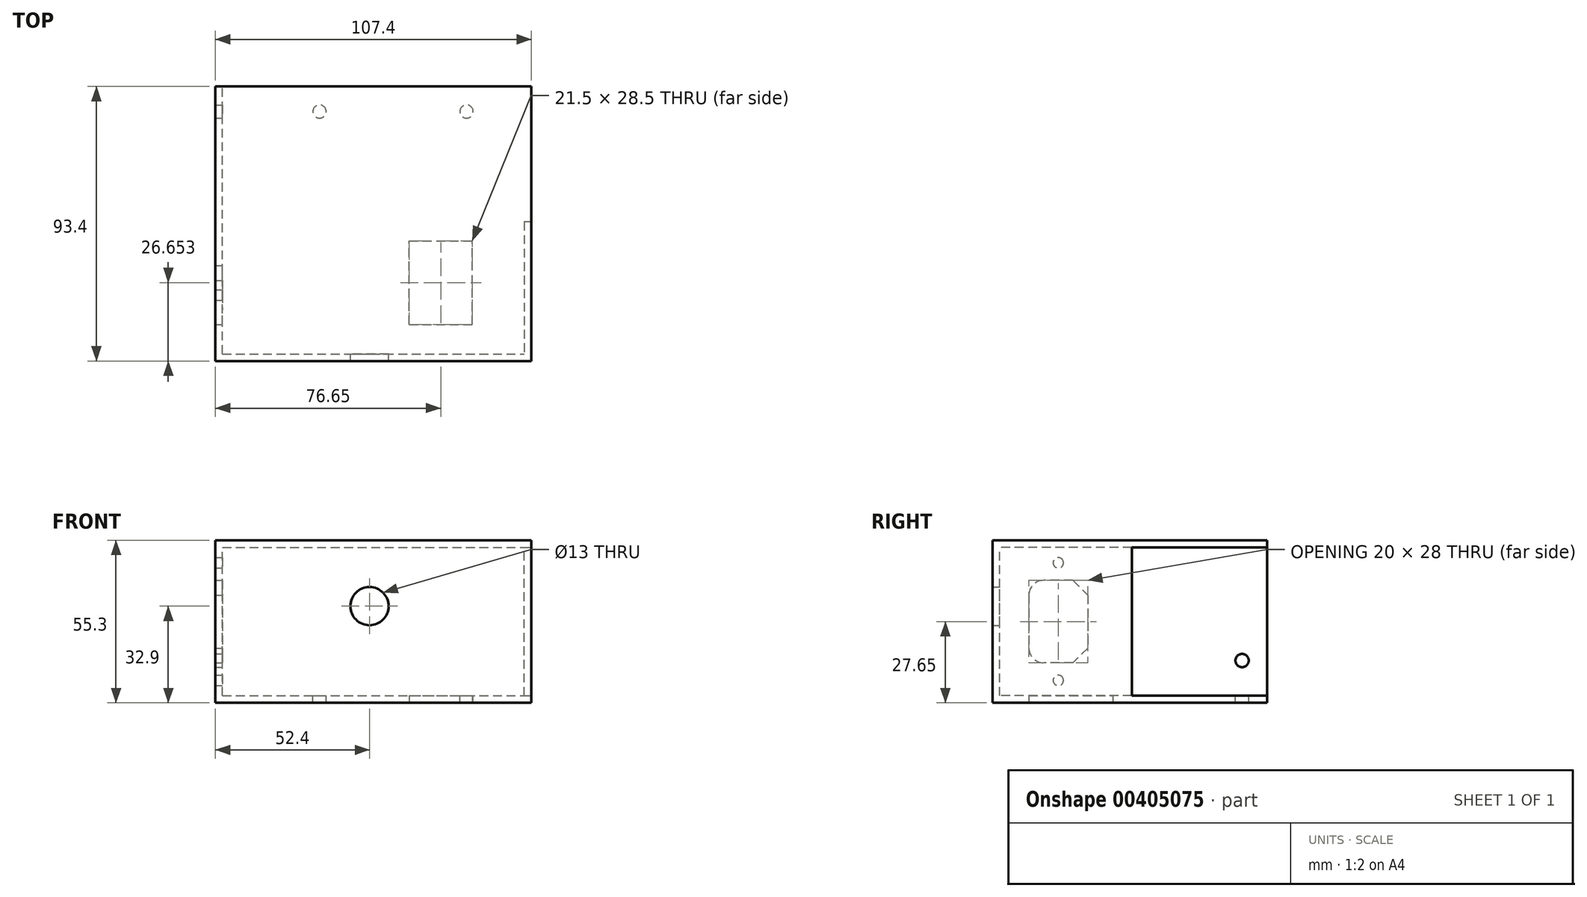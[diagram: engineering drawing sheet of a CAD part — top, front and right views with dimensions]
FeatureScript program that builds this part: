
annotation { "Feature Type Name" : "Feature", "Feature Type Description" : "" }
export const myFeature = defineFeature(function(context is Context, id is Id, definition is map)
    precondition{}
    {
        {
            var Q0;
            Q0=qCreatedBy(makeId("Front.planeOp"),FACE);
            var sketch = newSketch(context, id + "F0", { "sketchPlane" : qUnion([Q0])});
            skLineSegment(sketch, "E0.bottom", {"start": v(-57.5, 25) * mm, "end": v(0, 25) * mm});
            skLineSegment(sketch, "E0.top", {"start": v(-57.5, -25) * mm, "end": v(0, -25) * mm});
            skLineSegment(sketch, "E0.left", {"start": v(-57.5, 25) * mm, "end": v(-57.5, -25) * mm});
            skLineSegment(sketch, "E0.right", {"start": v(0, 25) * mm, "end": v(0, -25) * mm});
            skLineSegment(sketch, "E1", {"start": v(0, 0) * mm, "end": v(0, 48.13) * mm, "construction": true});
            skLineSegment(sketch, "E2", {"start": v(0, 0) * mm, "end": v(-98.9, 0) * mm, "construction": true});
            skPoint(sketch, "E2.endSnap0", {"position": v(0, 0) * mm});
            skSolve(sketch);
        }
        {
            var Q0;
            Q0=makeQuery(id+"F0.imprint","IMPRINT",FACE,{"disambiguationData":[TD([[makeQuery(id+"F0.imprint","IMPRINT",EDGE,{"derivedFrom":sQuery(id+"F0.wireOp",EDGE,"E0.bottom")}),-1.0]])]});
            extrude(context, id + "F1", {"entities" : qUnion([Q0]), "endBound" : BoundingType.SYMMETRIC, "depth" : 215 * mm});
        }
        {
            var Q0;
            Q0=makeQuery(id+"F1.opExtrude","SWEPT_FACE",FACE,{"disambiguationData":[OSD([sQuery(id+"F0.wireOp",EDGE,"E0.bottom")])]});
            var sketch = newSketch(context, id + "F2", { "sketchPlane" : qUnion([Q0])});
            skLineSegment(sketch, "E3.bottom", {"start": v(0, -107.5) * mm, "end": v(-55.8, -107.5) * mm});
            skLineSegment(sketch, "E3.top", {"start": v(0, -88.5) * mm, "end": v(-55.8, -88.5) * mm});
            skLineSegment(sketch, "E3.left", {"start": v(0, -107.5) * mm, "end": v(0, -88.5) * mm});
            skLineSegment(sketch, "E3.right", {"start": v(-55.8, -107.5) * mm, "end": v(-55.8, -88.5) * mm});
            skSolve(sketch);
        }
        {
            var Q0;
            Q0=makeQuery(id+"F2.imprint","IMPRINT",FACE,{"disambiguationData":[TD([[makeQuery(id+"F2.imprint","IMPRINT",EDGE,{"derivedFrom":sQuery(id+"F2.wireOp",EDGE,"E3.bottom")}),1.0]])]});
            extrude(context, id + "F3", {"entities" : qUnion([Q0]), "operationType" : NewBodyOperationType.REMOVE, "oppositeDirection" : true, "depth" : 42 * mm});
        }
        {
            var Q0;
            Q0=makeQuery(id+"F1.opExtrude","SWEPT_FACE",FACE,{"disambiguationData":[OSD([sQuery(id+"F0.wireOp",EDGE,"E0.bottom")])]});
            var sketch = newSketch(context, id + "F4", { "sketchPlane" : qUnion([Q0])});
            skLineSegment(sketch, "E4", {"start": v(-55.8, -107.5) * mm, "end": v(-55.8, 107.5) * mm});
            skLineSegment(sketch, "E5", {"start": v(-55.8, 107.5) * mm, "end": v(-55.5, 107.5) * mm});
            skLineSegment(sketch, "E6", {"start": v(-55.5, 107.5) * mm, "end": v(-55.5, 105.8) * mm});
            skLineSegment(sketch, "E7", {"start": v(-55.5, 105.8) * mm, "end": v(0, 105.8) * mm});
            skLineSegment(sketch, "E8", {"start": v(0, 105.8) * mm, "end": v(0, 105.5) * mm});
            skLineSegment(sketch, "E9", {"start": v(0, 105.5) * mm, "end": v(-55.5, 105.5) * mm});
            skLineSegment(sketch, "E10", {"start": v(-55.5, 105.5) * mm, "end": v(-55.5, -107.5) * mm});
            skLineSegment(sketch, "E11", {"start": v(-55.5, -107.5) * mm, "end": v(-55.8, -107.5) * mm});
            skSolve(sketch);
        }
        {
            var Q0;
            {var subQ1=sQuery(id+"F4.wireOp",EDGE,"E5");Q0=makeQuery(id+"F4.imprint","IMPRINT",FACE,{"disambiguationData":[TD([[makeQuery(id+"F4.imprint","IMPRINT",EDGE,{"derivedFrom":subQ1}),-1.0]])]});}
            var Q1;
            {var subQ0=sQuery(id+"F4.wireOp",EDGE,"E11");Q1=makeQuery(id+"F4.imprint","IMPRINT",FACE,{"disambiguationData":[TD([[makeQuery(id+"F4.imprint","IMPRINT",EDGE,{"derivedFrom":subQ0}),-1.0]])]});}
            extrude(context, id + "F5", {"entities" : qUnion([Q0, Q1]), "operationType" : NewBodyOperationType.REMOVE, "oppositeDirection" : true, "depth" : 48.3 * mm});
        }
        {
            var Q0;
            Q0=makeQuery(id+"F3.boolean.opBoolean","COPY",EDGE,{"derivedFrom":makeQuery(id+"F3.opExtrude","CAP_EDGE",EDGE,{"disambiguationData":[OSD([sQuery(id+"F2.wireOp",EDGE,"E3.top")])],"isStart":true})});
            var Q1;
            Q1=makeQuery(id+"F1.opExtrude","CAP_EDGE",EDGE,{"disambiguationData":[OSD([sQuery(id+"F0.wireOp",EDGE,"E0.top")])],"isStart":false});
            var Q2;
            Q2=makeQuery(id+"F1.opExtrude","SWEPT_EDGE",EDGE,{"disambiguationData":[OSD([sQuery(id+"F0.wireOp",EDGE,"E0.top"),sQuery(id+"F0.wireOp",EDGE,"E0.left")])]});
            var Q3;
            Q3=makeQuery(id+"F1.opExtrude","CAP_EDGE",EDGE,{"disambiguationData":[OSD([sQuery(id+"F0.wireOp",EDGE,"E0.top")])],"isStart":true});
            var Q4;
            Q4=makeQuery(id+"F1.opExtrude","CAP_EDGE",EDGE,{"disambiguationData":[OSD([sQuery(id+"F0.wireOp",EDGE,"E0.bottom")])],"isStart":false});
            var Q5;
            {var subQ0=sQuery(id+"F0.wireOp",EDGE,"E0.bottom");var subQ1=sQuery(id+"F0.wireOp",EDGE,"E0.left");Q5=makeQuery(id+"F5.boolean.opBoolean","SPLIT",EDGE,{"disambiguationData":[TD([makeQuery(id+"F1.opExtrude","SWEPT_FACE",FACE,{"disambiguationData":[OSD([subQ1])]})])],"derivedFrom":makeQuery(id+"F1.opExtrude","CAP_EDGE",EDGE,{"disambiguationData":[OSD([subQ0])],"isStart":true})});}
            var Q6;
            Q6=makeQuery(id+"F5.boolean.opBoolean","COPY",EDGE,{"derivedFrom":makeQuery(id+"F5.opExtrude","CAP_EDGE",EDGE,{"disambiguationData":[OSD([sQuery(id+"F4.wireOp",EDGE,"E6")])],"isStart":true})});
            var Q7;
            Q7=makeQuery(id+"F5.boolean.opBoolean","COPY",EDGE,{"derivedFrom":makeQuery(id+"F5.opExtrude","CAP_EDGE",EDGE,{"disambiguationData":[OSD([sQuery(id+"F4.wireOp",EDGE,"E9")])],"isStart":true})});
            var Q8;
            Q8=makeQuery(id+"F5.boolean.opBoolean","COPY",EDGE,{"derivedFrom":makeQuery(id+"F5.opExtrude","CAP_EDGE",EDGE,{"disambiguationData":[OSD([sQuery(id+"F4.wireOp",EDGE,"E10")])],"isStart":true})});
            fillet(context, id + "F6", {"entities" : qUnion([Q0, Q1, Q2, Q3, Q4, Q5, Q6, Q7, Q8]), "radius" : 2 * mm, "tangentPropagation" : true, "allowEdgeOverflow" : false});
        }
        {
            var Q0;
            Q0=makeQuery(id+"F1.opExtrude","SWEPT_BODY",BODY,{"disambiguationData":[OSD([sQuery(id+"F0.wireOp",EDGE,"E0.bottom"),sQuery(id+"F0.wireOp",EDGE,"E0.top"),sQuery(id+"F0.wireOp",EDGE,"E0.left"),sQuery(id+"F0.wireOp",EDGE,"E0.right")])]});
            var Q1;
            Q1=qCreatedBy(makeId("Right.planeOp"),FACE);
            mirror(context, id + "F7", {"operationType" : NewBodyOperationType.ADD, "entities" : qUnion([Q0]), "mirrorPlane" : qUnion([Q1])});
        }
        {
            var Q0;
            {var subQ0=makeQuery(id+"F3.boolean.opBoolean","COPY",FACE,{"derivedFrom":makeQuery(id+"F3.opExtrude","CAP_FACE",FACE,{"disambiguationData":[OSD([sQuery(id+"F2.wireOp",EDGE,"E3.bottom"),sQuery(id+"F2.wireOp",EDGE,"E3.top"),sQuery(id+"F2.wireOp",EDGE,"E3.left"),sQuery(id+"F2.wireOp",EDGE,"E3.right")])],"isStart":false})});Q0=makeQuery(id+"F7.boolean.opBoolean","MERGE",FACE,{"derivedFrom":[subQ0,makeQuery(id+"F7.opPattern","COPY",FACE,{"derivedFrom":subQ0,"instanceName":"1"})]});}
            var sketch = newSketch(context, id + "F8", { "sketchPlane" : qUnion([Q0])});
            skLineSegment(sketch, "E12.bottom", {"start": v(-34.2, -88.5) * mm, "end": v(52.8, -88.5) * mm});
            skLineSegment(sketch, "E12.top", {"start": v(-34.2, -103.8) * mm, "end": v(52.8, -103.8) * mm});
            skLineSegment(sketch, "E12.left", {"start": v(-34.2, -88.5) * mm, "end": v(-34.2, -103.8) * mm});
            skLineSegment(sketch, "E12.right", {"start": v(52.8, -88.5) * mm, "end": v(52.8, -103.8) * mm});
            skSolve(sketch);
        }
        {
            var Q0;
            Q0=makeQuery(id+"F8.imprint","IMPRINT",FACE,{"disambiguationData":[TD([[makeQuery(id+"F8.imprint","IMPRINT",EDGE,{"derivedFrom":sQuery(id+"F8.wireOp",EDGE,"E12.bottom")}),1.0]])]});
            extrude(context, id + "F9", {"entities" : qUnion([Q0]), "depth" : 14 * mm});
        }
        {
            var Q0;
            Q0=makeQuery(id+"F9.opExtrude","CAP_FACE",FACE,{"disambiguationData":[OSD([sQuery(id+"F8.wireOp",EDGE,"E12.bottom"),sQuery(id+"F8.wireOp",EDGE,"E12.top"),sQuery(id+"F8.wireOp",EDGE,"E12.left"),sQuery(id+"F8.wireOp",EDGE,"E12.right")])],"isStart":false});
            var sketch = newSketch(context, id + "F10", { "sketchPlane" : qUnion([Q0])});
            skLineSegment(sketch, "E13", {"start": v(-32.8, -103.8) * mm, "end": v(-32.8, -89.8) * mm});
            skLineSegment(sketch, "E14", {"start": v(-32.8, -89.8) * mm, "end": v(-24.6, -89.8) * mm});
            skLineSegment(sketch, "E15", {"start": v(-24.6, -89.8) * mm, "end": v(-24.6, -103.8) * mm});
            skLineSegment(sketch, "E16", {"start": v(-24.6, -103.8) * mm, "end": v(-32.8, -103.8) * mm});
            skLineSegment(sketch, "E17.1.0.0", {"start": v(-23.3, -103.8) * mm, "end": v(-23.3, -89.8) * mm});
            skLineSegment(sketch, "E17.1.0.1", {"start": v(-15.1, -103.8) * mm, "end": v(-23.3, -103.8) * mm});
            skLineSegment(sketch, "E17.1.0.2", {"start": v(-15.1, -89.8) * mm, "end": v(-15.1, -103.8) * mm});
            skLineSegment(sketch, "E17.1.0.3", {"start": v(-23.3, -89.8) * mm, "end": v(-15.1, -89.8) * mm});
            skLineSegment(sketch, "E17.2.0.0", {"start": v(-13.8, -103.8) * mm, "end": v(-13.8, -89.8) * mm});
            skLineSegment(sketch, "E17.2.0.1", {"start": v(-5.6, -103.8) * mm, "end": v(-13.8, -103.8) * mm});
            skLineSegment(sketch, "E17.2.0.2", {"start": v(-5.6, -89.8) * mm, "end": v(-5.6, -103.8) * mm});
            skLineSegment(sketch, "E17.2.0.3", {"start": v(-13.8, -89.8) * mm, "end": v(-5.6, -89.8) * mm});
            skLineSegment(sketch, "E17.3.0.0", {"start": v(-4.3, -103.8) * mm, "end": v(-4.3, -89.8) * mm});
            skLineSegment(sketch, "E17.3.0.1", {"start": v(3.9, -103.8) * mm, "end": v(-4.3, -103.8) * mm});
            skLineSegment(sketch, "E17.3.0.2", {"start": v(3.9, -89.8) * mm, "end": v(3.9, -103.8) * mm});
            skLineSegment(sketch, "E17.3.0.3", {"start": v(-4.3, -89.8) * mm, "end": v(3.9, -89.8) * mm});
            skLineSegment(sketch, "E17.4.0.0", {"start": v(5.2, -103.8) * mm, "end": v(5.2, -89.8) * mm});
            skLineSegment(sketch, "E17.4.0.1", {"start": v(13.4, -103.8) * mm, "end": v(5.2, -103.8) * mm});
            skLineSegment(sketch, "E17.4.0.2", {"start": v(13.4, -89.8) * mm, "end": v(13.4, -103.8) * mm});
            skLineSegment(sketch, "E17.4.0.3", {"start": v(5.2, -89.8) * mm, "end": v(13.4, -89.8) * mm});
            skLineSegment(sketch, "E17.5.0.0", {"start": v(14.7, -103.8) * mm, "end": v(14.7, -89.8) * mm});
            skLineSegment(sketch, "E17.5.0.1", {"start": v(22.9, -103.8) * mm, "end": v(14.7, -103.8) * mm});
            skLineSegment(sketch, "E17.5.0.2", {"start": v(22.9, -89.8) * mm, "end": v(22.9, -103.8) * mm});
            skLineSegment(sketch, "E17.5.0.3", {"start": v(14.7, -89.8) * mm, "end": v(22.9, -89.8) * mm});
            skLineSegment(sketch, "E17.6.0.0", {"start": v(24.2, -103.8) * mm, "end": v(24.2, -89.8) * mm});
            skLineSegment(sketch, "E17.6.0.1", {"start": v(32.4, -103.8) * mm, "end": v(24.2, -103.8) * mm});
            skLineSegment(sketch, "E17.6.0.2", {"start": v(32.4, -89.8) * mm, "end": v(32.4, -103.8) * mm});
            skLineSegment(sketch, "E17.6.0.3", {"start": v(24.2, -89.8) * mm, "end": v(32.4, -89.8) * mm});
            skLineSegment(sketch, "E17.7.0.0", {"start": v(33.7, -103.8) * mm, "end": v(33.7, -89.8) * mm});
            skLineSegment(sketch, "E17.7.0.1", {"start": v(41.9, -103.8) * mm, "end": v(33.7, -103.8) * mm});
            skLineSegment(sketch, "E17.7.0.2", {"start": v(41.9, -89.8) * mm, "end": v(41.9, -103.8) * mm});
            skLineSegment(sketch, "E17.7.0.3", {"start": v(33.7, -89.8) * mm, "end": v(41.9, -89.8) * mm});
            skLineSegment(sketch, "E17.8.0.0", {"start": v(43.2, -103.8) * mm, "end": v(43.2, -89.8) * mm});
            skLineSegment(sketch, "E17.8.0.1", {"start": v(51.4, -103.8) * mm, "end": v(43.2, -103.8) * mm});
            skLineSegment(sketch, "E17.8.0.2", {"start": v(51.4, -89.8) * mm, "end": v(51.4, -103.8) * mm});
            skLineSegment(sketch, "E17.8.0.3", {"start": v(43.2, -89.8) * mm, "end": v(51.4, -89.8) * mm});
            skLineSegment(sketch, "E17.direction1", {"start": v(-32.8, -103.8) * mm, "end": v(-23.3, -103.8) * mm, "construction": true});
            skSolve(sketch);
        }
        {
            var Q0;
            Q0=makeQuery(id+"F10.imprint","IMPRINT",FACE,{"disambiguationData":[TD([[makeQuery(id+"F10.imprint","IMPRINT",EDGE,{"derivedFrom":sQuery(id+"F10.wireOp",EDGE,"E13")}),-1.0]])]});
            var Q1;
            Q1=makeQuery(id+"F10.imprint","IMPRINT",FACE,{"disambiguationData":[TD([[makeQuery(id+"F10.imprint","IMPRINT",EDGE,{"derivedFrom":sQuery(id+"F10.wireOp",EDGE,"E17.1.0.0")}),-1.0]])]});
            var Q2;
            Q2=makeQuery(id+"F10.imprint","IMPRINT",FACE,{"disambiguationData":[TD([[makeQuery(id+"F10.imprint","IMPRINT",EDGE,{"derivedFrom":sQuery(id+"F10.wireOp",EDGE,"E17.2.0.0")}),-1.0]])]});
            var Q3;
            Q3=makeQuery(id+"F10.imprint","IMPRINT",FACE,{"disambiguationData":[TD([[makeQuery(id+"F10.imprint","IMPRINT",EDGE,{"derivedFrom":sQuery(id+"F10.wireOp",EDGE,"E17.3.0.0")}),-1.0]])]});
            var Q4;
            Q4=makeQuery(id+"F10.imprint","IMPRINT",FACE,{"disambiguationData":[TD([[makeQuery(id+"F10.imprint","IMPRINT",EDGE,{"derivedFrom":sQuery(id+"F10.wireOp",EDGE,"E17.4.0.0")}),-1.0]])]});
            var Q5;
            Q5=makeQuery(id+"F10.imprint","IMPRINT",FACE,{"disambiguationData":[TD([[makeQuery(id+"F10.imprint","IMPRINT",EDGE,{"derivedFrom":sQuery(id+"F10.wireOp",EDGE,"E17.5.0.0")}),-1.0]])]});
            var Q6;
            Q6=makeQuery(id+"F10.imprint","IMPRINT",FACE,{"disambiguationData":[TD([[makeQuery(id+"F10.imprint","IMPRINT",EDGE,{"derivedFrom":sQuery(id+"F10.wireOp",EDGE,"E17.6.0.0")}),-1.0]])]});
            var Q7;
            Q7=makeQuery(id+"F10.imprint","IMPRINT",FACE,{"disambiguationData":[TD([[makeQuery(id+"F10.imprint","IMPRINT",EDGE,{"derivedFrom":sQuery(id+"F10.wireOp",EDGE,"E17.7.0.0")}),-1.0]])]});
            var Q8;
            Q8=makeQuery(id+"F10.imprint","IMPRINT",FACE,{"disambiguationData":[TD([[makeQuery(id+"F10.imprint","IMPRINT",EDGE,{"derivedFrom":sQuery(id+"F10.wireOp",EDGE,"E17.8.0.0")}),-1.0]])]});
            extrude(context, id + "F11", {"entities" : qUnion([Q0, Q1, Q2, Q3, Q4, Q5, Q6, Q7, Q8]), "operationType" : NewBodyOperationType.REMOVE, "oppositeDirection" : true, "depth" : 7.4 * mm});
        }
        {
            var Q0;
            {var subQ0=sQuery(id+"F8.wireOp",EDGE,"E12.left");var subQ1=sQuery(id+"F8.wireOp",EDGE,"E12.top");Q0=makeQuery(id+"F11.boolean.opBoolean","SPLIT",EDGE,{"disambiguationData":[TD([makeQuery(id+"F9.opExtrude","SWEPT_FACE",FACE,{"disambiguationData":[OSD([subQ0])]})])],"derivedFrom":makeQuery(id+"F9.opExtrude","CAP_EDGE",EDGE,{"disambiguationData":[OSD([subQ1])],"isStart":false})});}
            var Q1;
            {var subQ0=sQuery(id+"F8.wireOp",EDGE,"E12.top");Q1=makeQuery(id+"F11.boolean.opBoolean","SPLIT",EDGE,{"disambiguationData":[TD([makeQuery(id+"F11.opExtrude","SWEPT_FACE",FACE,{"disambiguationData":[OSD([sQuery(id+"F10.wireOp",EDGE,"E15")])]})])],"derivedFrom":makeQuery(id+"F9.opExtrude","CAP_EDGE",EDGE,{"disambiguationData":[OSD([subQ0])],"isStart":false})});}
            var Q2;
            {var subQ0=sQuery(id+"F8.wireOp",EDGE,"E12.top");Q2=makeQuery(id+"F11.boolean.opBoolean","SPLIT",EDGE,{"disambiguationData":[TD([makeQuery(id+"F11.opExtrude","SWEPT_FACE",FACE,{"disambiguationData":[OSD([sQuery(id+"F10.wireOp",EDGE,"E17.1.0.2")])]})])],"derivedFrom":makeQuery(id+"F9.opExtrude","CAP_EDGE",EDGE,{"disambiguationData":[OSD([subQ0])],"isStart":false})});}
            var Q3;
            {var subQ0=sQuery(id+"F8.wireOp",EDGE,"E12.top");Q3=makeQuery(id+"F11.boolean.opBoolean","SPLIT",EDGE,{"disambiguationData":[TD([makeQuery(id+"F11.opExtrude","SWEPT_FACE",FACE,{"disambiguationData":[OSD([sQuery(id+"F10.wireOp",EDGE,"E17.2.0.2")])]})])],"derivedFrom":makeQuery(id+"F9.opExtrude","CAP_EDGE",EDGE,{"disambiguationData":[OSD([subQ0])],"isStart":false})});}
            var Q4;
            {var subQ0=sQuery(id+"F8.wireOp",EDGE,"E12.top");Q4=makeQuery(id+"F11.boolean.opBoolean","SPLIT",EDGE,{"disambiguationData":[TD([makeQuery(id+"F11.opExtrude","SWEPT_FACE",FACE,{"disambiguationData":[OSD([sQuery(id+"F10.wireOp",EDGE,"E17.3.0.2")])]})])],"derivedFrom":makeQuery(id+"F9.opExtrude","CAP_EDGE",EDGE,{"disambiguationData":[OSD([subQ0])],"isStart":false})});}
            var Q5;
            {var subQ0=sQuery(id+"F8.wireOp",EDGE,"E12.top");Q5=makeQuery(id+"F11.boolean.opBoolean","SPLIT",EDGE,{"disambiguationData":[TD([makeQuery(id+"F11.opExtrude","SWEPT_FACE",FACE,{"disambiguationData":[OSD([sQuery(id+"F10.wireOp",EDGE,"E17.4.0.2")])]})])],"derivedFrom":makeQuery(id+"F9.opExtrude","CAP_EDGE",EDGE,{"disambiguationData":[OSD([subQ0])],"isStart":false})});}
            var Q6;
            {var subQ0=sQuery(id+"F8.wireOp",EDGE,"E12.top");Q6=makeQuery(id+"F11.boolean.opBoolean","SPLIT",EDGE,{"disambiguationData":[TD([makeQuery(id+"F11.opExtrude","SWEPT_FACE",FACE,{"disambiguationData":[OSD([sQuery(id+"F10.wireOp",EDGE,"E17.5.0.2")])]})])],"derivedFrom":makeQuery(id+"F9.opExtrude","CAP_EDGE",EDGE,{"disambiguationData":[OSD([subQ0])],"isStart":false})});}
            var Q7;
            {var subQ0=sQuery(id+"F8.wireOp",EDGE,"E12.top");Q7=makeQuery(id+"F11.boolean.opBoolean","SPLIT",EDGE,{"disambiguationData":[TD([makeQuery(id+"F11.opExtrude","SWEPT_FACE",FACE,{"disambiguationData":[OSD([sQuery(id+"F10.wireOp",EDGE,"E17.6.0.2")])]})])],"derivedFrom":makeQuery(id+"F9.opExtrude","CAP_EDGE",EDGE,{"disambiguationData":[OSD([subQ0])],"isStart":false})});}
            var Q8;
            {var subQ0=sQuery(id+"F8.wireOp",EDGE,"E12.top");Q8=makeQuery(id+"F11.boolean.opBoolean","SPLIT",EDGE,{"disambiguationData":[TD([makeQuery(id+"F11.opExtrude","SWEPT_FACE",FACE,{"disambiguationData":[OSD([sQuery(id+"F10.wireOp",EDGE,"E17.7.0.2")])]})])],"derivedFrom":makeQuery(id+"F9.opExtrude","CAP_EDGE",EDGE,{"disambiguationData":[OSD([subQ0])],"isStart":false})});}
            var Q9;
            {var subQ0=sQuery(id+"F8.wireOp",EDGE,"E12.right");var subQ1=sQuery(id+"F8.wireOp",EDGE,"E12.top");Q9=makeQuery(id+"F11.boolean.opBoolean","SPLIT",EDGE,{"disambiguationData":[TD([makeQuery(id+"F9.opExtrude","SWEPT_FACE",FACE,{"disambiguationData":[OSD([subQ0])]})])],"derivedFrom":makeQuery(id+"F9.opExtrude","CAP_EDGE",EDGE,{"disambiguationData":[OSD([subQ1])],"isStart":false})});}
            fillet(context, id + "F12", {"entities" : qUnion([Q0, Q1, Q2, Q3, Q4, Q5, Q6, Q7, Q8, Q9]), "radius" : 2 * mm, "tangentPropagation" : true, "allowEdgeOverflow" : false});
        }
        {
            var Q0;
            Q0=makeQuery(id+"F11.boolean.opBoolean","COPY",FACE,{"derivedFrom":makeQuery(id+"F11.opExtrude","CAP_FACE",FACE,{"disambiguationData":[OSD([sQuery(id+"F10.wireOp",EDGE,"E13"),sQuery(id+"F10.wireOp",EDGE,"E14"),sQuery(id+"F10.wireOp",EDGE,"E15"),sQuery(id+"F10.wireOp",EDGE,"E16")])],"isStart":false})});
            var sketch = newSketch(context, id + "F13", { "sketchPlane" : qUnion([Q0])});
            skLineSegment(sketch, "E18", {"start": v(-32.8, -89.8) * mm, "end": v(-24.6, -103.8) * mm, "construction": true});
            skCircle(sketch, "E19", {"center": v(-28.7, -96.8) * mm, "radius": 2.5 * mm});
            skCircle(sketch, "E20.1.0.0", {"center": v(-19.2, -96.8) * mm, "radius": 2.5 * mm});
            skCircle(sketch, "E20.2.0.0", {"center": v(-9.7, -96.8) * mm, "radius": 2.5 * mm});
            skCircle(sketch, "E20.3.0.0", {"center": v(-0.2, -96.8) * mm, "radius": 2.5 * mm});
            skCircle(sketch, "E20.4.0.0", {"center": v(9.3, -96.8) * mm, "radius": 2.5 * mm});
            skCircle(sketch, "E20.5.0.0", {"center": v(18.8, -96.8) * mm, "radius": 2.5 * mm});
            skCircle(sketch, "E20.6.0.0", {"center": v(28.3, -96.8) * mm, "radius": 2.5 * mm});
            skCircle(sketch, "E20.7.0.0", {"center": v(37.8, -96.8) * mm, "radius": 2.5 * mm});
            skCircle(sketch, "E20.8.0.0", {"center": v(47.3, -96.8) * mm, "radius": 2.5 * mm});
            skLineSegment(sketch, "E20.direction1", {"start": v(-28.7, -96.8) * mm, "end": v(-19.2, -96.8) * mm, "construction": true});
            skSolve(sketch);
        }
        {
            var Q0;
            Q0=makeQuery(id+"F13.imprint","IMPRINT",FACE,{"disambiguationData":[TD([[makeQuery(id+"F13.imprint","IMPRINT",EDGE,{"derivedFrom":sQuery(id+"F13.wireOp",EDGE,"E19")}),1.0]])]});
            var Q1;
            Q1=makeQuery(id+"F13.imprint","IMPRINT",FACE,{"disambiguationData":[TD([[makeQuery(id+"F13.imprint","IMPRINT",EDGE,{"derivedFrom":sQuery(id+"F13.wireOp",EDGE,"E20.1.0.0")}),1.0]])]});
            var Q2;
            Q2=makeQuery(id+"F13.imprint","IMPRINT",FACE,{"disambiguationData":[TD([[makeQuery(id+"F13.imprint","IMPRINT",EDGE,{"derivedFrom":sQuery(id+"F13.wireOp",EDGE,"E20.2.0.0")}),1.0]])]});
            var Q3;
            Q3=makeQuery(id+"F13.imprint","IMPRINT",FACE,{"disambiguationData":[TD([[makeQuery(id+"F13.imprint","IMPRINT",EDGE,{"derivedFrom":sQuery(id+"F13.wireOp",EDGE,"E20.3.0.0")}),1.0]])]});
            var Q4;
            Q4=makeQuery(id+"F13.imprint","IMPRINT",FACE,{"disambiguationData":[TD([[makeQuery(id+"F13.imprint","IMPRINT",EDGE,{"derivedFrom":sQuery(id+"F13.wireOp",EDGE,"E20.4.0.0")}),1.0]])]});
            var Q5;
            Q5=makeQuery(id+"F13.imprint","IMPRINT",FACE,{"disambiguationData":[TD([[makeQuery(id+"F13.imprint","IMPRINT",EDGE,{"derivedFrom":sQuery(id+"F13.wireOp",EDGE,"E20.5.0.0")}),1.0]])]});
            var Q6;
            Q6=makeQuery(id+"F13.imprint","IMPRINT",FACE,{"disambiguationData":[TD([[makeQuery(id+"F13.imprint","IMPRINT",EDGE,{"derivedFrom":sQuery(id+"F13.wireOp",EDGE,"E20.6.0.0")}),1.0]])]});
            var Q7;
            Q7=makeQuery(id+"F13.imprint","IMPRINT",FACE,{"disambiguationData":[TD([[makeQuery(id+"F13.imprint","IMPRINT",EDGE,{"derivedFrom":sQuery(id+"F13.wireOp",EDGE,"E20.7.0.0")}),1.0]])]});
            var Q8;
            Q8=makeQuery(id+"F13.imprint","IMPRINT",FACE,{"disambiguationData":[TD([[makeQuery(id+"F13.imprint","IMPRINT",EDGE,{"derivedFrom":sQuery(id+"F13.wireOp",EDGE,"E20.8.0.0")}),1.0]])]});
            var Q9;
            Q9=sQuery(id+"F13.wireOp",EDGE,"E19");
            extrude(context, id + "F14", {"entities" : qUnion([Q0, Q1, Q2, Q3, Q4, Q5, Q6, Q7, Q8]), "operationType" : NewBodyOperationType.ADD, "surfaceEntities" : qUnion([Q9]), "depth" : 4 * mm});
        }
        {
            var Q0;
            Q0=makeQuery(id+"F14.opExtrude","CAP_EDGE",EDGE,{"disambiguationData":[OSD([sQuery(id+"F13.wireOp",EDGE,"E19")])],"isStart":false});
            var Q1;
            Q1=makeQuery(id+"F14.opExtrude","CAP_EDGE",EDGE,{"disambiguationData":[OSD([sQuery(id+"F13.wireOp",EDGE,"E20.1.0.0")])],"isStart":false});
            var Q2;
            Q2=makeQuery(id+"F14.opExtrude","CAP_EDGE",EDGE,{"disambiguationData":[OSD([sQuery(id+"F13.wireOp",EDGE,"E20.2.0.0")])],"isStart":false});
            var Q3;
            Q3=makeQuery(id+"F14.opExtrude","CAP_EDGE",EDGE,{"disambiguationData":[OSD([sQuery(id+"F13.wireOp",EDGE,"E20.3.0.0")])],"isStart":false});
            var Q4;
            Q4=makeQuery(id+"F14.opExtrude","CAP_EDGE",EDGE,{"disambiguationData":[OSD([sQuery(id+"F13.wireOp",EDGE,"E20.4.0.0")])],"isStart":false});
            var Q5;
            Q5=makeQuery(id+"F14.opExtrude","CAP_EDGE",EDGE,{"disambiguationData":[OSD([sQuery(id+"F13.wireOp",EDGE,"E20.5.0.0")])],"isStart":false});
            var Q6;
            Q6=makeQuery(id+"F14.opExtrude","CAP_EDGE",EDGE,{"disambiguationData":[OSD([sQuery(id+"F13.wireOp",EDGE,"E20.6.0.0")])],"isStart":false});
            var Q7;
            Q7=makeQuery(id+"F14.opExtrude","CAP_EDGE",EDGE,{"disambiguationData":[OSD([sQuery(id+"F13.wireOp",EDGE,"E20.7.0.0")])],"isStart":false});
            var Q8;
            Q8=makeQuery(id+"F14.opExtrude","CAP_EDGE",EDGE,{"disambiguationData":[OSD([sQuery(id+"F13.wireOp",EDGE,"E20.8.0.0")])],"isStart":false});
            fillet(context, id + "F15", {"entities" : qUnion([Q0, Q1, Q2, Q3, Q4, Q5, Q6, Q7, Q8]), "radius" : 1 * mm, "tangentPropagation" : true, "allowEdgeOverflow" : false});
        }
        {
            var Q0;
            Q0=makeQuery(id+"F1.opExtrude","SWEPT_FACE",FACE,{"disambiguationData":[OSD([sQuery(id+"F0.wireOp",EDGE,"E0.left")])]});
            var sketch = newSketch(context, id + "F16", { "sketchPlane" : qUnion([Q0])});
            skLineSegment(sketch, "E21", {"start": v(-75, -13) * mm, "end": v(75, -13) * mm});
            skLineSegment(sketch, "E22", {"start": v(0, 0) * mm, "end": v(0, -13) * mm});
            skSolve(sketch);
        }
        {
            var Q0;
            Q0=makeQuery(id+"F7.opPattern","COPY",FACE,{"derivedFrom":makeQuery(id+"F1.opExtrude","SWEPT_FACE",FACE,{"disambiguationData":[OSD([sQuery(id+"F0.wireOp",EDGE,"E0.left")])]}),"instanceName":"1"});
            var sketch = newSketch(context, id + "F17", { "sketchPlane" : qUnion([Q0])});
            skPoint(sketch, "E23.0", {"position": v(-75, -13) * mm});
            skPoint(sketch, "E23.1", {"position": v(75, -13) * mm});
            skPoint(sketch, "E24", {"position": v(-75, 12) * mm});
            skPoint(sketch, "E25", {"position": v(75, 12) * mm});
            skSolve(sketch);
        }
        {
            var Q0;
            {var subQ0=makeQuery(id+"F1.opExtrude","SWEPT_FACE",FACE,{"disambiguationData":[OSD([sQuery(id+"F0.wireOp",EDGE,"E0.top")])]});Q0=makeQuery(id+"F7.boolean.opBoolean","MERGE",FACE,{"derivedFrom":[subQ0,makeQuery(id+"F7.opPattern","COPY",FACE,{"derivedFrom":subQ0,"instanceName":"1"})]});}
            var sketch = newSketch(context, id + "F18", { "sketchPlane" : qUnion([Q0])});
            skLineSegment(sketch, "E26", {"start": v(-21.97, 0) * mm, "end": v(0, 0) * mm, "construction": true});
            skLineSegment(sketch, "E27", {"start": v(0, 0) * mm, "end": v(0, 32.91) * mm, "construction": true});
            skPoint(sketch, "E28", {"position": v(-25, 75) * mm});
            skPoint(sketch, "E29.MirrorP", {"position": v(-25, -75) * mm});
            skPoint(sketch, "E30.MirrorP", {"position": v(25, -75) * mm});
            skPoint(sketch, "E31.MirrorP", {"position": v(25, 75) * mm});
            skSolve(sketch);
        }
        {
            var Q0;
            Q0=sQuery(id+"F16.wireOp",VERTEX,"E21.start");
            var Q1;
            Q1=sQuery(id+"F16.wireOp",VERTEX,"E21.end");
            var Q2;
            Q2=sQuery(id+"F18.wireOp",VERTEX,"E29.MirrorP");
            var Q3;
            Q3=sQuery(id+"F18.wireOp",VERTEX,"E28");
            var Q4;
            Q4=sQuery(id+"F18.wireOp",VERTEX,"E30.MirrorP");
            var Q5;
            Q5=sQuery(id+"F18.wireOp",VERTEX,"E31.MirrorP");
            var Q6;
            Q6=sQuery(id+"F17.wireOp",VERTEX,"E23.0");
            var Q7;
            Q7=sQuery(id+"F17.wireOp",VERTEX,"E24");
            var Q8;
            Q8=sQuery(id+"F17.wireOp",VERTEX,"E25");
            var Q9;
            Q9=sQuery(id+"F17.wireOp",VERTEX,"E23.1");
            var Q10;
            Q10=makeQuery(id+"F1.opExtrude","SWEPT_BODY",BODY,{"disambiguationData":[OSD([sQuery(id+"F0.wireOp",EDGE,"E0.bottom"),sQuery(id+"F0.wireOp",EDGE,"E0.top"),sQuery(id+"F0.wireOp",EDGE,"E0.left"),sQuery(id+"F0.wireOp",EDGE,"E0.right")])]});
            hole(context, id + "F19", {"style" : HoleStyle.SIMPLE, "endStyle" : HoleEndStyle.BLIND, "holeDiameter" : 3.3 * mm, "holeDepth" : 5 * mm, "locations" : qUnion([Q0, Q1, Q2, Q3, Q4, Q5, Q6, Q7, Q8, Q9]), "scope" : qUnion([Q10])});
        }
        {
            var Q0;
            Q0=makeQuery(id+"F7.opPattern","COPY",FACE,{"derivedFrom":makeQuery(id+"F1.opExtrude","SWEPT_FACE",FACE,{"disambiguationData":[OSD([sQuery(id+"F0.wireOp",EDGE,"E0.left")])]}),"instanceName":"1"});
            var sketch = newSketch(context, id + "F20", { "sketchPlane" : qUnion([Q0])});
            skLineSegment(sketch, "E32.bottom", {"start": v(-156.5, 25) * mm, "end": v(107.5, 25) * mm});
            skLineSegment(sketch, "E32.top", {"start": v(-156.5, -25) * mm, "end": v(107.5, -25) * mm});
            skLineSegment(sketch, "E32.left", {"start": v(-156.5, 25) * mm, "end": v(-156.5, -25) * mm});
            skLineSegment(sketch, "E32.right", {"start": v(107.5, 25) * mm, "end": v(107.5, -25) * mm});
            skCircle(sketch, "E33", {"center": v(-75, 12) * mm, "radius": 1.5 * mm});
            skCircle(sketch, "E34", {"center": v(-75, -13) * mm, "radius": 1.5 * mm});
            skCircle(sketch, "E35", {"center": v(75, -13) * mm, "radius": 1.5 * mm});
            skCircle(sketch, "E36", {"center": v(75, 12) * mm, "radius": 1.5 * mm});
            skSolve(sketch);
        }
        {
            var Q0;
            Q0 = qSketchRegion(id + "F20", true);
            extrude(context, id + "F21", {"entities" : qUnion([Q0]), "depth" : 6 * mm});
        }
        {
            var Q0;
            {var subQ0=makeQuery(id+"F1.opExtrude","SWEPT_FACE",FACE,{"disambiguationData":[OSD([sQuery(id+"F0.wireOp",EDGE,"E0.top")])]});Q0=makeQuery(id+"F7.boolean.opBoolean","MERGE",FACE,{"derivedFrom":[subQ0,makeQuery(id+"F7.opPattern","COPY",FACE,{"derivedFrom":subQ0,"instanceName":"1"})]});}
            var sketch = newSketch(context, id + "F22", { "sketchPlane" : qUnion([Q0])});
            skLineSegment(sketch, "E37.bottom", {"start": v(-58, 157.48) * mm, "end": v(64, 157.48) * mm});
            skLineSegment(sketch, "E37.top", {"start": v(-58, 66.48) * mm, "end": v(64, 66.48) * mm});
            skLineSegment(sketch, "E37.left", {"start": v(-58, 157.48) * mm, "end": v(-58, 66.48) * mm});
            skLineSegment(sketch, "E37.right", {"start": v(64, 157.48) * mm, "end": v(64, 66.48) * mm});
            skCircle(sketch, "E38", {"center": v(-25, 75) * mm, "radius": 2.25 * mm});
            skCircle(sketch, "E39", {"center": v(25, 75) * mm, "radius": 2.25 * mm});
            skSolve(sketch);
        }
        {
            var Q0;
            Q0 = qSketchRegion(id + "F22", true);
            extrude(context, id + "F23", {"entities" : qUnion([Q0]), "depth" : 2.4 * mm});
        }
        {
            var Q0;
            Q0=makeQuery(id+"F23.opExtrude","SWEPT_FACE",FACE,{"disambiguationData":[OSD([sQuery(id+"F22.wireOp",EDGE,"E37.left")])]});
            var sketch = newSketch(context, id + "F24", { "sketchPlane" : qUnion([Q0])});
            skLineSegment(sketch, "E40.bottom", {"start": v(157.48, -27.4) * mm, "end": v(66.48, -27.4) * mm});
            skLineSegment(sketch, "E40.top", {"start": v(157.48, 25.5) * mm, "end": v(66.48, 25.5) * mm});
            skLineSegment(sketch, "E40.left", {"start": v(157.48, -27.4) * mm, "end": v(157.48, 25.5) * mm});
            skLineSegment(sketch, "E40.right", {"start": v(66.48, -27.4) * mm, "end": v(66.48, 25.5) * mm});
            skLineSegment(sketch, "E41.bottom", {"start": v(132.48, 14.25) * mm, "end": v(142.48, 14.25) * mm});
            skLineSegment(sketch, "E41.top", {"start": v(132.48, -13.75) * mm, "end": v(142.48, -13.75) * mm});
            skLineSegment(sketch, "E41.left", {"start": v(127.48, 9.25) * mm, "end": v(127.48, -8.75) * mm});
            skLineSegment(sketch, "E41.right", {"start": v(147.48, 9.25) * mm, "end": v(147.48, -8.75) * mm});
            skPoint(sketch, "E42.visualSharp", {"position": v(147.48, 14.25) * mm});
            skArc(sketch, "E42.filletArc", {"start": v(147.48, 9.25) * mm, "mid": v(146.01, 12.79) * mm, "end": v(142.48, 14.25) * mm});
            skPoint(sketch, "E43.visualSharp", {"position": v(147.48, -13.75) * mm});
            skArc(sketch, "E43.filletArc", {"start": v(142.48, -13.75) * mm, "mid": v(146.01, -12.29) * mm, "end": v(147.48, -8.75) * mm});
            skLineSegment(sketch, "E44", {"start": v(132.48, 14.25) * mm, "end": v(127.48, 9.25) * mm});
            skLineSegment(sketch, "E45", {"start": v(127.48, -8.75) * mm, "end": v(132.48, -13.75) * mm});
            skLineSegment(sketch, "E46", {"start": v(137.48, 20.25) * mm, "end": v(137.48, -19.75) * mm, "construction": true});
            skPoint(sketch, "E46.endSnap0", {"position": v(137.48, -13.75) * mm});
            skCircle(sketch, "E47", {"center": v(137.48, 20.25) * mm, "radius": 1.75 * mm});
            skCircle(sketch, "E48", {"center": v(137.48, -19.75) * mm, "radius": 1.75 * mm});
            skSolve(sketch);
        }
        {
            var Q0;
            Q0 = qSketchRegion(id + "F24", true);
            extrude(context, id + "F25", {"entities" : qUnion([Q0]), "operationType" : NewBodyOperationType.ADD, "depth" : 2.4 * mm});
        }
        {
            var Q0;
            Q0=makeQuery(id+"F1.opExtrude","SWEPT_FACE",FACE,{"disambiguationData":[OSD([sQuery(id+"F0.wireOp",EDGE,"E0.left")])]});
            var sketch = newSketch(context, id + "F26", { "sketchPlane" : qUnion([Q0])});
            skCircle(sketch, "E49", {"center": v(75, -13) * mm, "radius": 2.25 * mm});
            skSolve(sketch);
        }
        {
            var Q0;
            Q0 = qSketchRegion(id + "F26", true);
            extrude(context, id + "F27", {"entities" : qUnion([Q0]), "operationType" : NewBodyOperationType.REMOVE, "depth" : 25 * mm});
        }
        {
            var Q0;
            Q0=makeQuery(id+"F23.opExtrude","SWEPT_FACE",FACE,{"disambiguationData":[OSD([sQuery(id+"F22.wireOp",EDGE,"E37.right")])]});
            var sketch = newSketch(context, id + "F28", { "sketchPlane" : qUnion([Q0])});
            skLineSegment(sketch, "E50.bottom", {"start": v(-157.48, -27.4) * mm, "end": v(-66.48, -27.4) * mm});
            skLineSegment(sketch, "E50.top", {"start": v(-157.48, 25.5) * mm, "end": v(-66.48, 25.5) * mm});
            skLineSegment(sketch, "E50.left", {"start": v(-157.48, -27.4) * mm, "end": v(-157.48, 25.5) * mm});
            skLineSegment(sketch, "E50.right", {"start": v(-66.48, -27.4) * mm, "end": v(-66.48, 25.5) * mm});
            skSolve(sketch);
        }
        {
            var Q0;
            Q0 = qSketchRegion(id + "F28", true);
            extrude(context, id + "F29", {"entities" : qUnion([Q0]), "operationType" : NewBodyOperationType.ADD, "depth" : 3 * mm});
        }
        {
            var Q0;
            Q0=makeQuery(id+"F21.opExtrude","CAP_FACE",FACE,{"disambiguationData":[OSD([sQuery(id+"F20.wireOp",EDGE,"E32.bottom"),sQuery(id+"F20.wireOp",EDGE,"E32.top"),sQuery(id+"F20.wireOp",EDGE,"E32.left"),sQuery(id+"F20.wireOp",EDGE,"E32.right"),sQuery(id+"F20.wireOp",EDGE,"E33"),sQuery(id+"F20.wireOp",EDGE,"E34"),sQuery(id+"F20.wireOp",EDGE,"E35"),sQuery(id+"F20.wireOp",EDGE,"E36")])],"isStart":false});
            var sketch = newSketch(context, id + "F30", { "sketchPlane" : qUnion([Q0])});
            skCircle(sketch, "E51", {"center": v(-75, 12) * mm, "radius": 1.75 * mm});
            skCircle(sketch, "E52", {"center": v(-75, -13) * mm, "radius": 1.75 * mm});
            skSolve(sketch);
        }
        {
            var Q0;
            Q0 = qSketchRegion(id + "F30", true);
            extrude(context, id + "F31", {"entities" : qUnion([Q0]), "operationType" : NewBodyOperationType.REMOVE, "depth" : 25 * mm});
        }
        {
            var Q0;
            Q0=makeQuery(id+"F25.opExtrude","SWEPT_FACE",FACE,{"disambiguationData":[OSD([sQuery(id+"F24.wireOp",EDGE,"E40.top")])]});
            var sketch = newSketch(context, id + "F32", { "sketchPlane" : qUnion([Q0])});
            skLineSegment(sketch, "E53.bottom", {"start": v(-60.4, -157.48) * mm, "end": v(67, -157.48) * mm});
            skLineSegment(sketch, "E53.top", {"start": v(-60.4, -66.48) * mm, "end": v(67, -66.48) * mm});
            skLineSegment(sketch, "E53.left", {"start": v(-60.4, -157.48) * mm, "end": v(-60.4, -66.48) * mm});
            skLineSegment(sketch, "E53.right", {"start": v(67, -157.48) * mm, "end": v(67, -66.48) * mm});
            skSolve(sketch);
        }
        {
            var Q0;
            Q0 = qSketchRegion(id + "F32", true);
            extrude(context, id + "F33", {"entities" : qUnion([Q0]), "operationType" : NewBodyOperationType.ADD, "depth" : 2.4 * mm});
        }
        {
            var Q0;
            Q0=makeQuery(id+"F33.boolean.opBoolean","MERGE",FACE,{"derivedFrom":[makeQuery(id+"F29.boolean.opBoolean","MERGE",FACE,{"derivedFrom":[makeQuery(id+"F25.boolean.opBoolean","MERGE",FACE,{"derivedFrom":[makeQuery(id+"F23.opExtrude","SWEPT_FACE",FACE,{"disambiguationData":[OSD([sQuery(id+"F22.wireOp",EDGE,"E37.bottom")])]}),makeQuery(id+"F25.opExtrude","SWEPT_FACE",FACE,{"disambiguationData":[OSD([sQuery(id+"F24.wireOp",EDGE,"E40.left")])]})]}),makeQuery(id+"F29.opExtrude","SWEPT_FACE",FACE,{"disambiguationData":[OSD([sQuery(id+"F28.wireOp",EDGE,"E50.left")])]})]}),makeQuery(id+"F33.opExtrude","SWEPT_FACE",FACE,{"disambiguationData":[OSD([sQuery(id+"F32.wireOp",EDGE,"E53.bottom")])]})]});
            var sketch = newSketch(context, id + "F34", { "sketchPlane" : qUnion([Q0])});
            skLineSegment(sketch, "E54.bottom", {"start": v(67, -27.4) * mm, "end": v(-60.4, -27.4) * mm});
            skLineSegment(sketch, "E54.top", {"start": v(67, 27.9) * mm, "end": v(-60.4, 27.9) * mm});
            skLineSegment(sketch, "E54.left", {"start": v(67, -27.4) * mm, "end": v(67, 27.9) * mm});
            skLineSegment(sketch, "E54.right", {"start": v(-60.4, -27.4) * mm, "end": v(-60.4, 27.9) * mm});
            skCircle(sketch, "E55", {"center": v(-8, 5.5) * mm, "radius": 6.5 * mm});
            skSolve(sketch);
        }
        {
            var Q0;
            Q0 = qSketchRegion(id + "F34", true);
            extrude(context, id + "F35", {"entities" : qUnion([Q0]), "operationType" : NewBodyOperationType.ADD, "depth" : 2.4 * mm});
        }
        {
            var Q0;
            Q0=makeQuery(id+"F35.boolean.opBoolean","MERGE",FACE,{"derivedFrom":[makeQuery(id+"F29.boolean.opBoolean","MERGE",FACE,{"derivedFrom":[makeQuery(id+"F25.boolean.opBoolean","MERGE",FACE,{"derivedFrom":[makeQuery(id+"F23.opExtrude","CAP_FACE",FACE,{"disambiguationData":[OSD([sQuery(id+"F22.wireOp",EDGE,"E37.bottom"),sQuery(id+"F22.wireOp",EDGE,"E37.top"),sQuery(id+"F22.wireOp",EDGE,"E37.left"),sQuery(id+"F22.wireOp",EDGE,"E37.right"),sQuery(id+"F22.wireOp",EDGE,"E38"),sQuery(id+"F22.wireOp",EDGE,"E39")])],"isStart":false}),makeQuery(id+"F25.opExtrude","SWEPT_FACE",FACE,{"disambiguationData":[OSD([sQuery(id+"F24.wireOp",EDGE,"E40.bottom")])]})]}),makeQuery(id+"F29.opExtrude","SWEPT_FACE",FACE,{"disambiguationData":[OSD([sQuery(id+"F28.wireOp",EDGE,"E50.bottom")])]})]}),makeQuery(id+"F35.opExtrude","SWEPT_FACE",FACE,{"disambiguationData":[OSD([sQuery(id+"F34.wireOp",EDGE,"E54.bottom")])]})]});
            var sketch = newSketch(context, id + "F36", { "sketchPlane" : qUnion([Q0])});
            skLineSegment(sketch, "E56.bottom", {"start": v(5.5, 147.48) * mm, "end": v(27, 147.48) * mm});
            skLineSegment(sketch, "E56.top", {"start": v(5.5, 118.98) * mm, "end": v(27, 118.98) * mm});
            skLineSegment(sketch, "E56.left", {"start": v(5.5, 147.48) * mm, "end": v(5.5, 118.98) * mm});
            skLineSegment(sketch, "E56.right", {"start": v(27, 147.48) * mm, "end": v(27, 118.98) * mm});
            skSolve(sketch);
        }
        {
            var Q0;
            Q0 = qSketchRegion(id + "F36", true);
            extrude(context, id + "F37", {"entities" : qUnion([Q0]), "operationType" : NewBodyOperationType.REMOVE, "oppositeDirection" : true, "depth" : 25 * mm});
        }
        {
            var Q0;
            Q0=makeQuery(id+"F35.boolean.opBoolean","MERGE",FACE,{"derivedFrom":[makeQuery(id+"F33.opExtrude","CAP_FACE",FACE,{"disambiguationData":[OSD([sQuery(id+"F32.wireOp",EDGE,"E53.bottom"),sQuery(id+"F32.wireOp",EDGE,"E53.top"),sQuery(id+"F32.wireOp",EDGE,"E53.left"),sQuery(id+"F32.wireOp",EDGE,"E53.right")])],"isStart":false}),makeQuery(id+"F35.opExtrude","SWEPT_FACE",FACE,{"disambiguationData":[OSD([sQuery(id+"F34.wireOp",EDGE,"E54.top")])]})]});
            var sketch = newSketch(context, id + "F38", { "sketchPlane" : qUnion([Q0])});
            skLineSegment(sketch, "E57.bottom", {"start": v(67, -159.88) * mm, "end": v(47, -159.88) * mm});
            skLineSegment(sketch, "E57.top", {"start": v(67, -59.88) * mm, "end": v(47, -59.88) * mm});
            skLineSegment(sketch, "E57.left", {"start": v(67, -159.88) * mm, "end": v(67, -59.88) * mm});
            skLineSegment(sketch, "E57.right", {"start": v(47, -159.88) * mm, "end": v(47, -59.88) * mm});
            skSolve(sketch);
        }
        {
            var Q0;
            Q0 = qSketchRegion(id + "F38", true);
            extrude(context, id + "F39", {"entities" : qUnion([Q0]), "operationType" : NewBodyOperationType.REMOVE, "oppositeDirection" : true, "depth" : 60 * mm});
        }
        {
            var Q0;
            Q0=makeQuery(id+"F1.opExtrude","SWEPT_BODY",BODY,{"disambiguationData":[OSD([sQuery(id+"F0.wireOp",EDGE,"E0.bottom"),sQuery(id+"F0.wireOp",EDGE,"E0.top"),sQuery(id+"F0.wireOp",EDGE,"E0.left"),sQuery(id+"F0.wireOp",EDGE,"E0.right")])]});
            deleteBodies(context, id + "F40", {"entities" : qUnion([Q0])});
        }
        {
            var Q0;
            Q0=makeQuery(id+"F9.opExtrude","SWEPT_BODY",BODY,{"disambiguationData":[OSD([sQuery(id+"F8.wireOp",EDGE,"E12.bottom"),sQuery(id+"F8.wireOp",EDGE,"E12.top"),sQuery(id+"F8.wireOp",EDGE,"E12.left"),sQuery(id+"F8.wireOp",EDGE,"E12.right")])]});
            deleteBodies(context, id + "F41", {"entities" : qUnion([Q0])});
        }
        {
            var Q0;
            Q0=makeQuery(id+"F21.opExtrude","SWEPT_BODY",BODY,{"disambiguationData":[OSD([sQuery(id+"F20.wireOp",EDGE,"E32.bottom"),sQuery(id+"F20.wireOp",EDGE,"E32.top"),sQuery(id+"F20.wireOp",EDGE,"E32.left"),sQuery(id+"F20.wireOp",EDGE,"E32.right"),sQuery(id+"F20.wireOp",EDGE,"E33"),sQuery(id+"F20.wireOp",EDGE,"E34"),sQuery(id+"F20.wireOp",EDGE,"E35"),sQuery(id+"F20.wireOp",EDGE,"E36")])]});
            deleteBodies(context, id + "F42", {"entities" : qUnion([Q0])});
        }
        {
            var Q0;
            Q0=makeQuery(id+"F35.opExtrude","CAP_FACE",FACE,{"disambiguationData":[OSD([sQuery(id+"F34.wireOp",EDGE,"E54.bottom"),sQuery(id+"F34.wireOp",EDGE,"E54.top"),sQuery(id+"F34.wireOp",EDGE,"E54.left"),sQuery(id+"F34.wireOp",EDGE,"E54.right"),sQuery(id+"F34.wireOp",EDGE,"E55")])],"isStart":true});
            var sketch = newSketch(context, id + "F43", { "sketchPlane" : qUnion([Q0])});
            skLineSegment(sketch, "E58.bottom", {"start": v(-47, -25) * mm, "end": v(-44.6, -25) * mm});
            skLineSegment(sketch, "E58.top", {"start": v(-47, 25.5) * mm, "end": v(-44.6, 25.5) * mm});
            skLineSegment(sketch, "E58.left", {"start": v(-47, -25) * mm, "end": v(-47, 25.5) * mm});
            skLineSegment(sketch, "E58.right", {"start": v(-44.6, -25) * mm, "end": v(-44.6, 25.5) * mm});
            skSolve(sketch);
        }
        {
            var Q0;
            Q0 = qSketchRegion(id + "F43", true);
            extrude(context, id + "F44", {"entities" : qUnion([Q0]), "operationType" : NewBodyOperationType.ADD, "depth" : 45 * mm});
        }
    });
